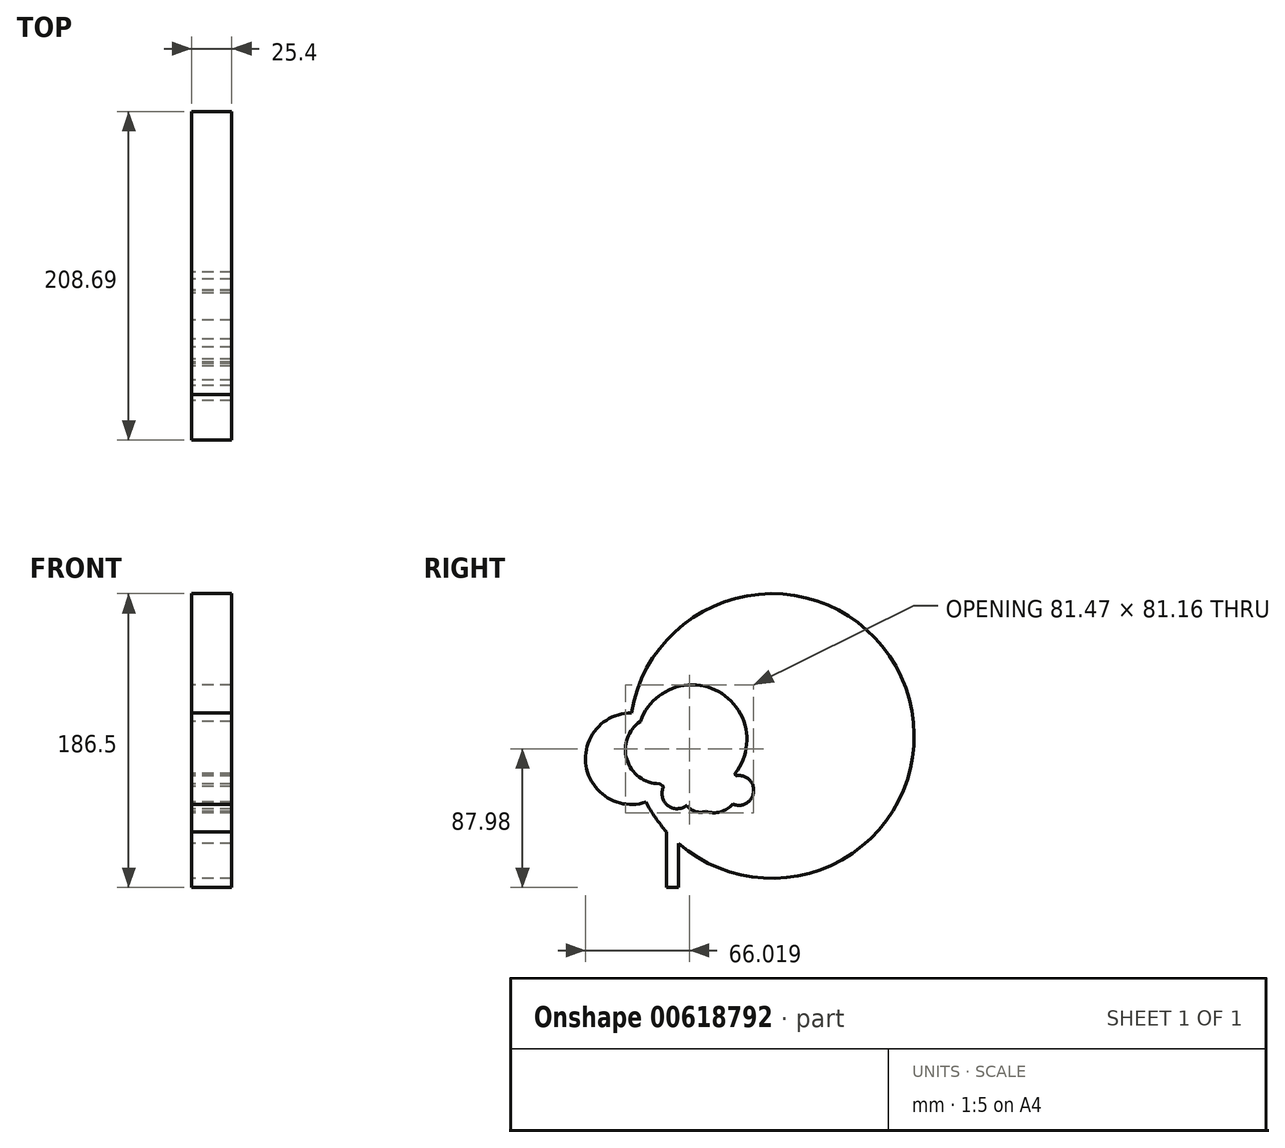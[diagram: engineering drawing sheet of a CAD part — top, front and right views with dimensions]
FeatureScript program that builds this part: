
annotation { "Feature Type Name" : "Feature", "Feature Type Description" : "" }
export const myFeature = defineFeature(function(context is Context, id is Id, definition is map)
    precondition{}
    {
        {
            var Q0;
            Q0=qCreatedBy(makeId("Right.planeOp"),FACE);
            var sketch = newSketch(context, id + "F0", { "sketchPlane" : qUnion([Q0])});
            skLineSegment(sketch, "E0.bottom", {"start": v(-22.88, -58) * mm, "end": v(-15.4, -58) * mm});
            skLineSegment(sketch, "E0.top", {"start": v(-22.88, 3.3) * mm, "end": v(-15.4, 3.3) * mm});
            skLineSegment(sketch, "E0.left", {"start": v(-22.88, -58) * mm, "end": v(-22.88, 3.3) * mm});
            skLineSegment(sketch, "E0.right", {"start": v(-15.4, -58) * mm, "end": v(-15.4, 3.3) * mm});
            skArc(sketch, "E1", {"start": v(-24.32, 6.76) * mm, "mid": v(-8.91, -4.61) * mm, "end": v(-22.88, 8.5) * mm});
            skCircle(sketch, "E2", {"center": v(6.76, 12.23) * mm, "radius": 13.98 * mm});
            skCircle(sketch, "E3", {"center": v(-1.58, -0.14) * mm, "radius": 10.22 * mm});
            skCircle(sketch, "E4", {"center": v(7.05, 5.32) * mm, "radius": 15.92 * mm});
            skCircle(sketch, "E5", {"center": v(22.88, 3.6) * mm, "radius": 9.5 * mm});
            skCircle(sketch, "E6", {"center": v(32.38, 3.89) * mm, "radius": 36.13 * mm});
            skCircle(sketch, "E7", {"center": v(43.9, 38.13) * mm, "radius": 90.37 * mm});
            skCircle(sketch, "E8", {"center": v(-45.33, 23.74) * mm, "radius": 29.1 * mm});
            skCircle(sketch, "E9", {"center": v(-27.49, 29.5) * mm, "radius": 21.67 * mm});
            skCircle(sketch, "E10", {"center": v(-6.76, 35.83) * mm, "radius": 34.83 * mm});
            skSolve(sketch);
        }
        {
            var Q0;
            {var subQ0=sQuery(id+"F0.wireOp",EDGE,"E0.bottom");Q0=makeQuery(id+"F0.imprint","IMPRINT",FACE,{"disambiguationData":[TD([[makeQuery(id+"F0.imprint","IMPRINT",EDGE,{"derivedFrom":subQ0}),1.0]])]});}
            var Q1;
            {var subQ0=sQuery(id+"F0.wireOp",EDGE,"E7");var subQ1=sQuery(id+"F0.wireOp",EDGE,"E0.left");var subQ2=makeQuery(id+"F0.imprint","INTERSECT",VERTEX,{"derivedFrom":[subQ1,subQ0]});Q1=makeQuery(id+"F0.imprint","IMPRINT",FACE,{"disambiguationData":[TD([[makeQuery(id+"F0.imprint","IMPRINT",EDGE,{"disambiguationData":[TD([[subQ2,-1.0]])],"derivedFrom":subQ1}),1.0]])]});}
            var Q2;
            {var subQ0=sQuery(id+"F0.wireOp",EDGE,"E8");var subQ1=sQuery(id+"F0.wireOp",EDGE,"E7");var subQ2=makeQuery(id+"F0.imprint","INTERSECT",VERTEX,{"disambiguationData":[OD(0.0)],"derivedFrom":[subQ1,subQ0]});Q2=makeQuery(id+"F0.imprint","IMPRINT",FACE,{"disambiguationData":[TD([[makeQuery(id+"F0.imprint","IMPRINT",EDGE,{"disambiguationData":[TD([[subQ2,-1.0]])],"derivedFrom":subQ1}),-1.0]])]});}
            var Q3;
            {var subQ0=sQuery(id+"F0.wireOp",EDGE,"E7");var subQ1=sQuery(id+"F0.wireOp",EDGE,"E0.left");var subQ2=makeQuery(id+"F0.imprint","INTERSECT",VERTEX,{"derivedFrom":[subQ1,subQ0]});Q3=makeQuery(id+"F0.imprint","IMPRINT",FACE,{"disambiguationData":[TD([[makeQuery(id+"F0.imprint","IMPRINT",EDGE,{"disambiguationData":[TD([[subQ2,-1.0]])],"derivedFrom":subQ1}),-1.0]])]});}
            var Q4;
            {var subQ0=sQuery(id+"F0.wireOp",EDGE,"E8");var subQ1=sQuery(id+"F0.wireOp",EDGE,"E7");var subQ2=makeQuery(id+"F0.imprint","INTERSECT",VERTEX,{"disambiguationData":[OD(0.0)],"derivedFrom":[subQ1,subQ0]});Q4=makeQuery(id+"F0.imprint","IMPRINT",FACE,{"disambiguationData":[TD([[makeQuery(id+"F0.imprint","IMPRINT",EDGE,{"disambiguationData":[TD([[subQ2,-1.0]])],"derivedFrom":subQ1}),1.0]])]});}
            var Q5;
            {var subQ3=sQuery(id+"F0.wireOp",EDGE,"E10");var subQ7=sQuery(id+"F0.wireOp",EDGE,"E1");var subQ8=makeQuery(id+"F0.imprint","INTERSECT",VERTEX,{"disambiguationData":[OD(0.0)],"derivedFrom":[subQ7,subQ3]});Q5=makeQuery(id+"F0.imprint","IMPRINT",FACE,{"disambiguationData":[TD([[makeQuery(id+"F0.imprint","IMPRINT",EDGE,{"disambiguationData":[TD([[subQ8,-1.0]])],"derivedFrom":subQ7}),-1.0]])]});}
            var Q6;
            {var subQ9=sQuery(id+"F0.wireOp",EDGE,"E0.right");var subQ11=sQuery(id+"F0.wireOp",EDGE,"E7");var subQ12=makeQuery(id+"F0.imprint","INTERSECT",VERTEX,{"derivedFrom":[subQ9,subQ11]});Q6=makeQuery(id+"F0.imprint","IMPRINT",FACE,{"disambiguationData":[TD([[makeQuery(id+"F0.imprint","IMPRINT",EDGE,{"disambiguationData":[TD([[subQ12,-1.0]])],"derivedFrom":subQ9}),-1.0]])]});}
            var Q7;
            {var subQ0=sQuery(id+"F0.wireOp",EDGE,"E4");var subQ5=sQuery(id+"F0.wireOp",EDGE,"E2");var subQ6=makeQuery(id+"F0.imprint","INTERSECT",VERTEX,{"disambiguationData":[OD(0.0)],"derivedFrom":[subQ5,subQ0]});Q7=makeQuery(id+"F0.imprint","IMPRINT",FACE,{"disambiguationData":[TD([[makeQuery(id+"F0.imprint","IMPRINT",EDGE,{"disambiguationData":[TD([[subQ6,-1.0]])],"derivedFrom":subQ5}),-1.0]])]});}
            extrude(context, id + "F1", {"entities" : qUnion([Q0, Q1, Q2, Q3, Q4, Q5, Q6, Q7]), "depth" : 25.4 * mm, "offsetDistance" : 25.4 * mm});
        }
    });
